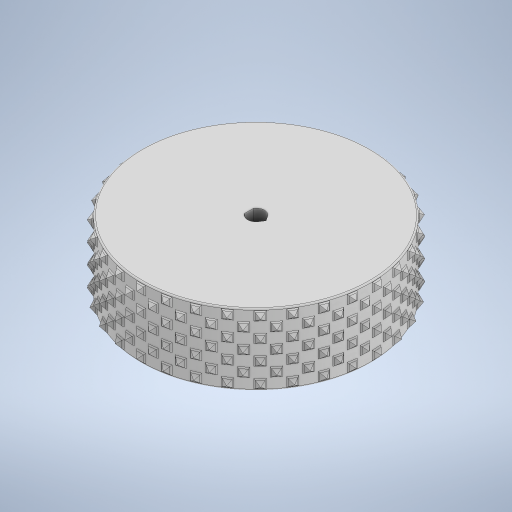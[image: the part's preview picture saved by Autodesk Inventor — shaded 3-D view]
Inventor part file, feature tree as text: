
AUTODESK INVENTOR PART (.ipt)
format: ipt  version: 2024.2 (Build 282272000, 272)  size: 12,293,632 bytes
history: native  units: in
note: dims shown in document units (in); Inventor stores cm internally (conversion verified against a paired STEP export)
features: chamfer x11, extrude x2, fillet x2, pattern_circular x2, sketch x2, plane x1
ambient origin geometry x8: Origin, YZ Plane, XZ Plane, XY Plane, X Axis, Y Axis, Z Axis, Center Point
bodies: Solid1 (feature_tree)
feature tree (20):
  extrude  "Extrusion1"  Depth=0.2362in
  plane  "Work Plane1"
  extrude  "Extrusion2"  Depth=1.0in TaperAngle=0.0deg
  chamfer  "Chamfer18"  Distance=0.125in
  fillet  "Fillet1"  Radius=0.125in
  pattern_circular  "Circular Pattern3"  [2 undecoded]
  fillet  "Fillet2"  Radius=0.125in
  chamfer  "Chamfer8"  Distance=0.15in
  chamfer  "Chamfer9"  Distance=0.125in
  chamfer  "Chamfer10"  Distance=0.125in
  chamfer  "Chamfer11"  Distance=0.15in
  chamfer  "Chamfer12"  Distance=0.125in
  chamfer  "Chamfer13"  Distance=0.125in
  chamfer  "Chamfer14"  Distance=0.15in
  chamfer  "Chamfer15"  Distance=0.5in
  chamfer  "Chamfer16"  Distance=0.1in Angle=45.0deg
  chamfer  "Chamfer17"  Distance=0.1in Angle=45.0deg
  pattern_circular  "Circular Pattern2"  Angle=45.0deg  [1 undecoded]
  sketch  "Sketch1"  dims[d0=3.2283in d1=0.2362in]
  sketch  "Sketch2"  dims[d2=0.2165in d3=1.0in d4=0.0in d5=0.125in d6=0.125in d7=0.125in d8=0.125in d9=0.15in d10=0.125in d11=0.125in d12=0.15in d16=0.125in d17=0.125in d19=0.15in d20=0.125in d21=0.125in d22=0.125in d23=0.125in d24=0.15in d25=0.125in d26=0.125in d27=0.15in d33=0.065in d34=0.0in d62=0.5in d63=0.1in d64=0.075in d65=45.0deg d66=0.1in d67=0.075in d68=45.0deg d69=0.1in d70=0.075in d71=45.0deg d72=0.1in d73=0.075in d74=45.0deg d75=0.1in d76=0.075in d77=45.0deg d78=0.1in d79=0.075in d80=45.0deg d81=0.1in d82=0.075in d83=45.0deg d84=0.1in d85=0.075in d86=45.0deg d87=0.1in d88=0.075in d89=45.0deg d90=0.1in d91=0.075in d92=45.0deg d93=9.4488in d94=360.0deg d96=0.0625in d97=0.0813in d99=0.1375in d100=0.0813in d101=0.0125in d102=0.0625in d103=0.125in d104=45.0deg d105=12.2047in d106=360.0deg d108=0.125in d109=0.0197in d107=0.0in]
note: 3 required parameter values undecoded (feature->parameter linkage not recoverable at this tier; creation-order binding heuristic only, values carry confidence <= 0.55)
